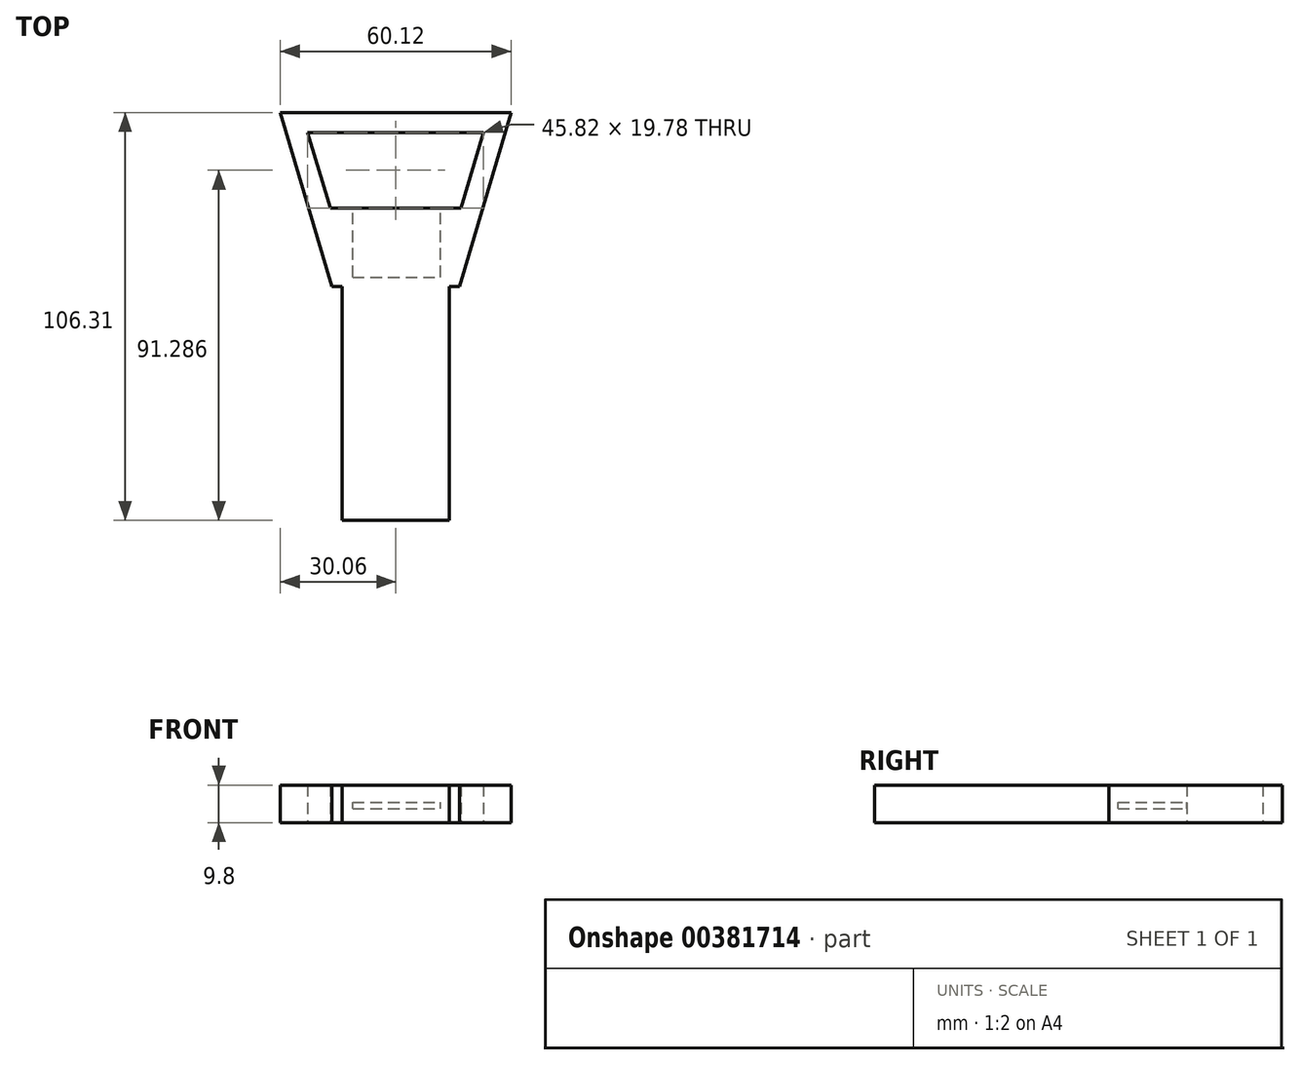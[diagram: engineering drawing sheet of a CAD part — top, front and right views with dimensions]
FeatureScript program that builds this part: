
annotation { "Feature Type Name" : "Feature", "Feature Type Description" : "" }
export const myFeature = defineFeature(function(context is Context, id is Id, definition is map)
    precondition{}
    {
        {
            var Q0;
            Q0=qCreatedBy(makeId("Top.planeOp"),FACE);
            var sketch = newSketch(context, id + "F0", { "sketchPlane" : qUnion([Q0])});
            skLineSegment(sketch, "E0", {"start": v(-30.06, 31.62) * mm, "end": v(-16.68, -13.66) * mm});
            skLineSegment(sketch, "E1", {"start": v(-16.68, -13.66) * mm, "end": v(0, -13.66) * mm});
            skLineSegment(sketch, "E2.MirrorCS", {"start": v(30.06, 31.62) * mm, "end": v(16.68, -13.66) * mm});
            skLineSegment(sketch, "E3.MirrorCS", {"start": v(16.68, -13.66) * mm, "end": v(0, -13.66) * mm});
            skLineSegment(sketch, "E4", {"start": v(-30.06, 31.62) * mm, "end": v(30.06, 31.62) * mm});
            skLineSegment(sketch, "E5", {"start": v(-22.91, 26.49) * mm, "end": v(-17.07, 6.7) * mm});
            skLineSegment(sketch, "E6", {"start": v(-17.07, 6.7) * mm, "end": v(0, 6.7) * mm});
            skLineSegment(sketch, "E7.MirrorCS", {"start": v(17.07, 6.7) * mm, "end": v(0, 6.7) * mm});
            skLineSegment(sketch, "E8.MirrorCS", {"start": v(22.91, 26.49) * mm, "end": v(17.07, 6.7) * mm});
            skLineSegment(sketch, "E9", {"start": v(-22.91, 26.49) * mm, "end": v(22.91, 26.49) * mm});
            skLineSegment(sketch, "E10", {"start": v(-13.93, -13.66) * mm, "end": v(-13.93, -74.7) * mm});
            skLineSegment(sketch, "E11", {"start": v(-13.93, -74.7) * mm, "end": v(0, -74.7) * mm});
            skLineSegment(sketch, "E12.MirrorCS", {"start": v(13.93, -74.7) * mm, "end": v(0, -74.7) * mm});
            skLineSegment(sketch, "E13.MirrorCS", {"start": v(13.93, -13.66) * mm, "end": v(13.93, -74.7) * mm});
            skSolve(sketch);
        }
        {
            var Q0;
            Q0 = qSketchRegion(id + "F0", true);
            extrude(context, id + "F1", {"entities" : qUnion([Q0]), "depth" : 9.8 * mm});
        }
        {
            var Q0;
            Q0=makeQuery(id+"F1.opExtrude","SWEPT_FACE",FACE,{"disambiguationData":[OSD([sQuery(id+"F0.wireOp",EDGE,"E6"),sQuery(id+"F0.wireOp",EDGE,"E7.MirrorCS")])]});
            var sketch = newSketch(context, id + "F2", { "sketchPlane" : qUnion([Q0])});
            skLineSegment(sketch, "E14.bottom", {"start": v(11.18, 3.65) * mm, "end": v(-11.72, 3.65) * mm});
            skLineSegment(sketch, "E14.top", {"start": v(11.18, 5.28) * mm, "end": v(-11.72, 5.28) * mm});
            skLineSegment(sketch, "E14.left", {"start": v(11.18, 3.65) * mm, "end": v(11.18, 5.28) * mm});
            skLineSegment(sketch, "E14.right", {"start": v(-11.72, 3.65) * mm, "end": v(-11.72, 5.28) * mm});
            skSolve(sketch);
        }
        {
            var Q0;
            Q0=makeQuery(id+"F2.imprint","IMPRINT",FACE,{"disambiguationData":[TD([[makeQuery(id+"F2.imprint","IMPRINT",EDGE,{"derivedFrom":sQuery(id+"F2.wireOp",EDGE,"E14.bottom")}),-1.0]])]});
            extrude(context, id + "F3", {"entities" : qUnion([Q0]), "operationType" : NewBodyOperationType.REMOVE, "oppositeDirection" : true, "depth" : 18 * mm});
        }
    });
